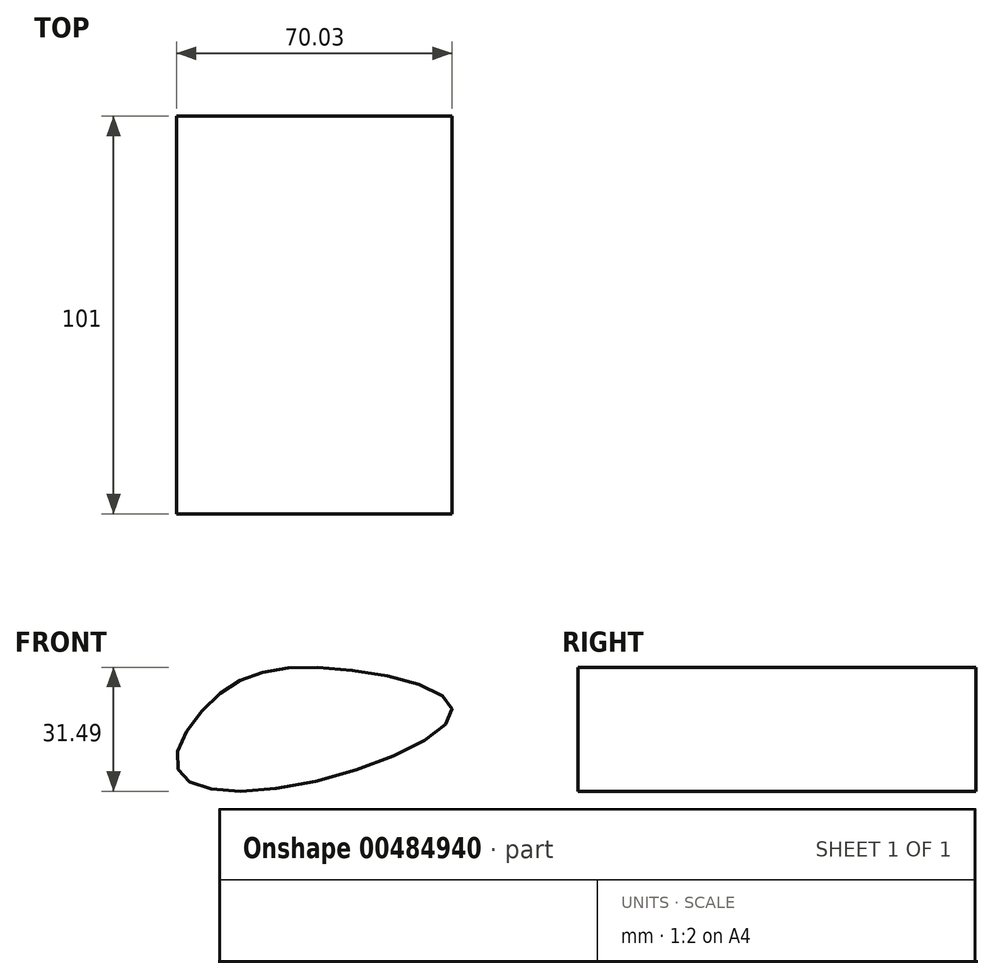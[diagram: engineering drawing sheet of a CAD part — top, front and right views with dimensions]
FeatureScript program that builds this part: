
annotation { "Feature Type Name" : "Feature", "Feature Type Description" : "" }
export const myFeature = defineFeature(function(context is Context, id is Id, definition is map)
    precondition{}
    {
        {
            var Q0;
            Q0=qCreatedBy(makeId("Front.planeOp"),FACE);
            var sketch = newSketch(context, id + "F0", { "sketchPlane" : qUnion([Q0])});
            skFitSpline(sketch, "E0", {"points": [v(-30.9, 3.9) * mm, v(-21.43, 22.14) * mm, v(5.33, 29.72) * mm, v(38.72, 19.3) * mm, v(0, 0) * mm, v(-30.9, 3.9) * mm]});
            skCircle(sketch, "E1", {"center": v(-33.51, 43.22) * mm, "radius": 7.01 * mm});
            skLineSegment(sketch, "E2.bottom", {"start": v(-8.64, 43.94) * mm, "end": v(12.2, 43.94) * mm});
            skLineSegment(sketch, "E2.top", {"start": v(-8.64, 56.73) * mm, "end": v(12.2, 56.73) * mm});
            skLineSegment(sketch, "E2.left", {"start": v(-8.64, 43.94) * mm, "end": v(-8.64, 56.73) * mm});
            skLineSegment(sketch, "E2.right", {"start": v(12.2, 43.94) * mm, "end": v(12.2, 56.73) * mm});
            skSolve(sketch);
        }
        {
            var Q0;
            Q0=makeQuery(id+"F0.imprint","IMPRINT",FACE,{"disambiguationData":[TD([[makeQuery(id+"F0.imprint","IMPRINT",EDGE,{"derivedFrom":sQuery(id+"F0.wireOp",EDGE,"E0")}),-1.0]])]});
            extrude(context, id + "F1", {"entities" : qUnion([Q0]), "depth" : 101 * mm});
        }
    });
